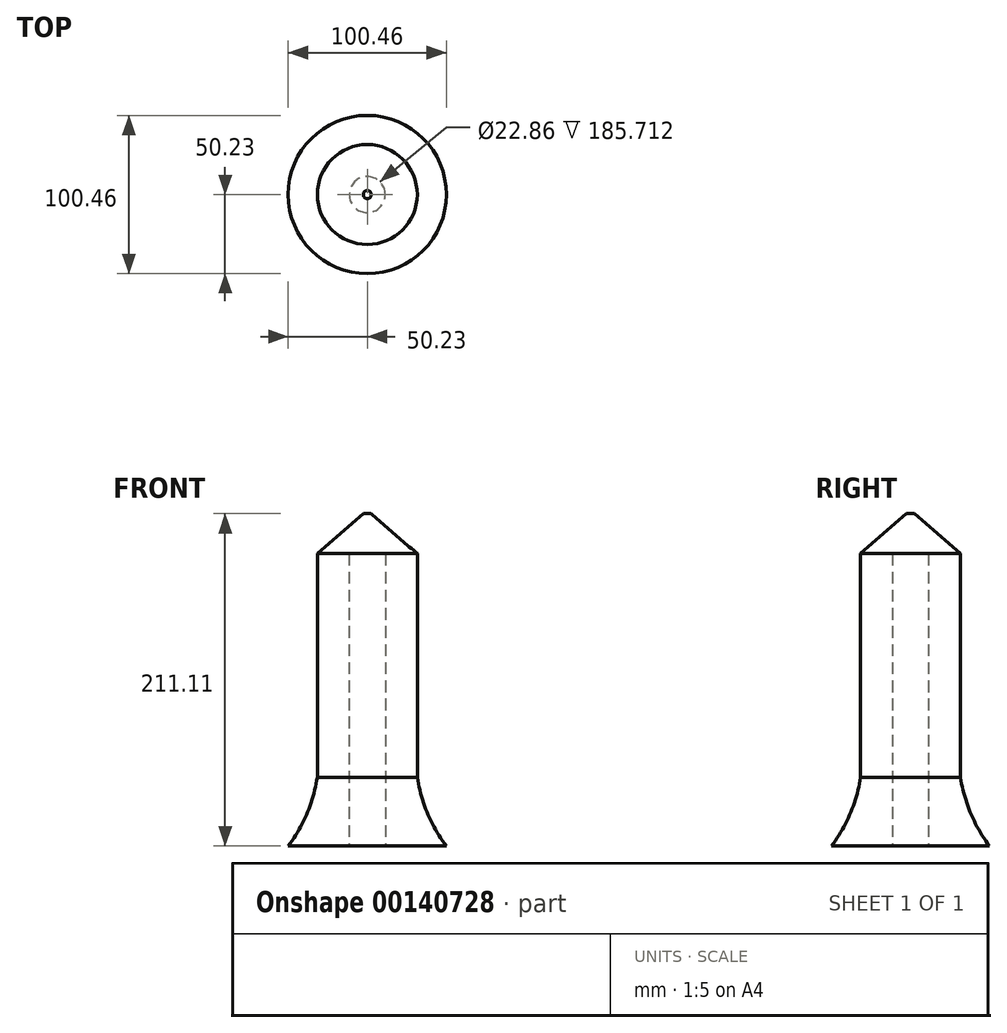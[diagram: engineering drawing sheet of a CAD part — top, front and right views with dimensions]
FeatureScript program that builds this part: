
annotation { "Feature Type Name" : "Feature", "Feature Type Description" : "" }
export const myFeature = defineFeature(function(context is Context, id is Id, definition is map)
    precondition{}
    {
        {
            var Q0;
            Q0=qCreatedBy(makeId("Top.planeOp"),FACE);
            var sketch = newSketch(context, id + "F0", { "sketchPlane" : qUnion([Q0])});
            skCircle(sketch, "E0", {"center": v(0, 0) * mm, "radius": 11.43 * mm});
            skCircle(sketch, "E1", {"center": v(0, 0) * mm, "radius": 31.75 * mm});
            skSolve(sketch);
        }
        {
            var Q0;
            Q0=makeQuery(id+"F0.imprint","IMPRINT",FACE,{"disambiguationData":[TD([[makeQuery(id+"F0.imprint","IMPRINT",EDGE,{"derivedFrom":sQuery(id+"F0.wireOp",EDGE,"E0")}),-1.0]])]});
            extrude(context, id + "F1", {"entities" : qUnion([Q0]), "depth" : 185.71 * mm});
        }
        {
            var Q0;
            Q0=qCreatedBy(makeId("Front.planeOp"),FACE);
            var sketch = newSketch(context, id + "F2", { "sketchPlane" : qUnion([Q0])});
            skLineSegment(sketch, "E2.bottom", {"start": v(-50.23, 0) * mm, "end": v(-30.65, 0) * mm});
            skLineSegment(sketch, "E2.left", {"start": v(-30.65, 0) * mm, "end": v(-30.65, 58.26) * mm});
            skArc(sketch, "E3", {"start": v(-50.23, 0) * mm, "mid": v(-35.68, 27.53) * mm, "end": v(-30.65, 58.26) * mm});
            skLineSegment(sketch, "E4", {"start": v(0, 76.12) * mm, "end": v(0, 0) * mm, "construction": true});
            skSolve(sketch);
        }
        {
            var Q0;
            Q0=makeQuery(id+"F2.imprint","IMPRINT",FACE,{"disambiguationData":[TD([[makeQuery(id+"F2.imprint","IMPRINT",EDGE,{"derivedFrom":sQuery(id+"F2.wireOp",EDGE,"E2.bottom")}),1.0]])]});
            var Q1;
            Q1 = qConstructionFilter(qBodyType(qCreatedBy(id + "F2" ,EDGE), BodyType.WIRE), ConstructionObject.NO);
            var Q2;
            Q2=sQuery(id+"F2.wireOp",EDGE,"E4");
            revolve(context, id + "F3", {"operationType" : NewBodyOperationType.ADD, "entities" : qUnion([Q0]), "surfaceEntities" : qUnion([Q1]), "axis" : qUnion([Q2]), "revolveType" : RevolveType.FULL});
        }
        {
            var Q0;
            Q0=makeQuery(id+"F1.opExtrude","CAP_FACE",FACE,{"disambiguationData":[OSD([sQuery(id+"F0.wireOp",EDGE,"E0"),sQuery(id+"F0.wireOp",EDGE,"E1")])],"isStart":false});
            var sketch = newSketch(context, id + "F4", { "sketchPlane" : qUnion([Q0])});
            skCircle(sketch, "E5.0", {"center": v(0, 0) * mm, "radius": 31.75 * mm});
            skSolve(sketch);
        }
        {
            var Q0;
            Q0 = qSketchRegion(id + "F4", true);
            extrude(context, id + "F5", {"entities" : qUnion([Q0]), "operationType" : NewBodyOperationType.ADD, "depth" : 25.4 * mm, "hasDraft" : true, "draftAngle" : 49 * degree, "draftPullDirection" : true});
        }
    });
